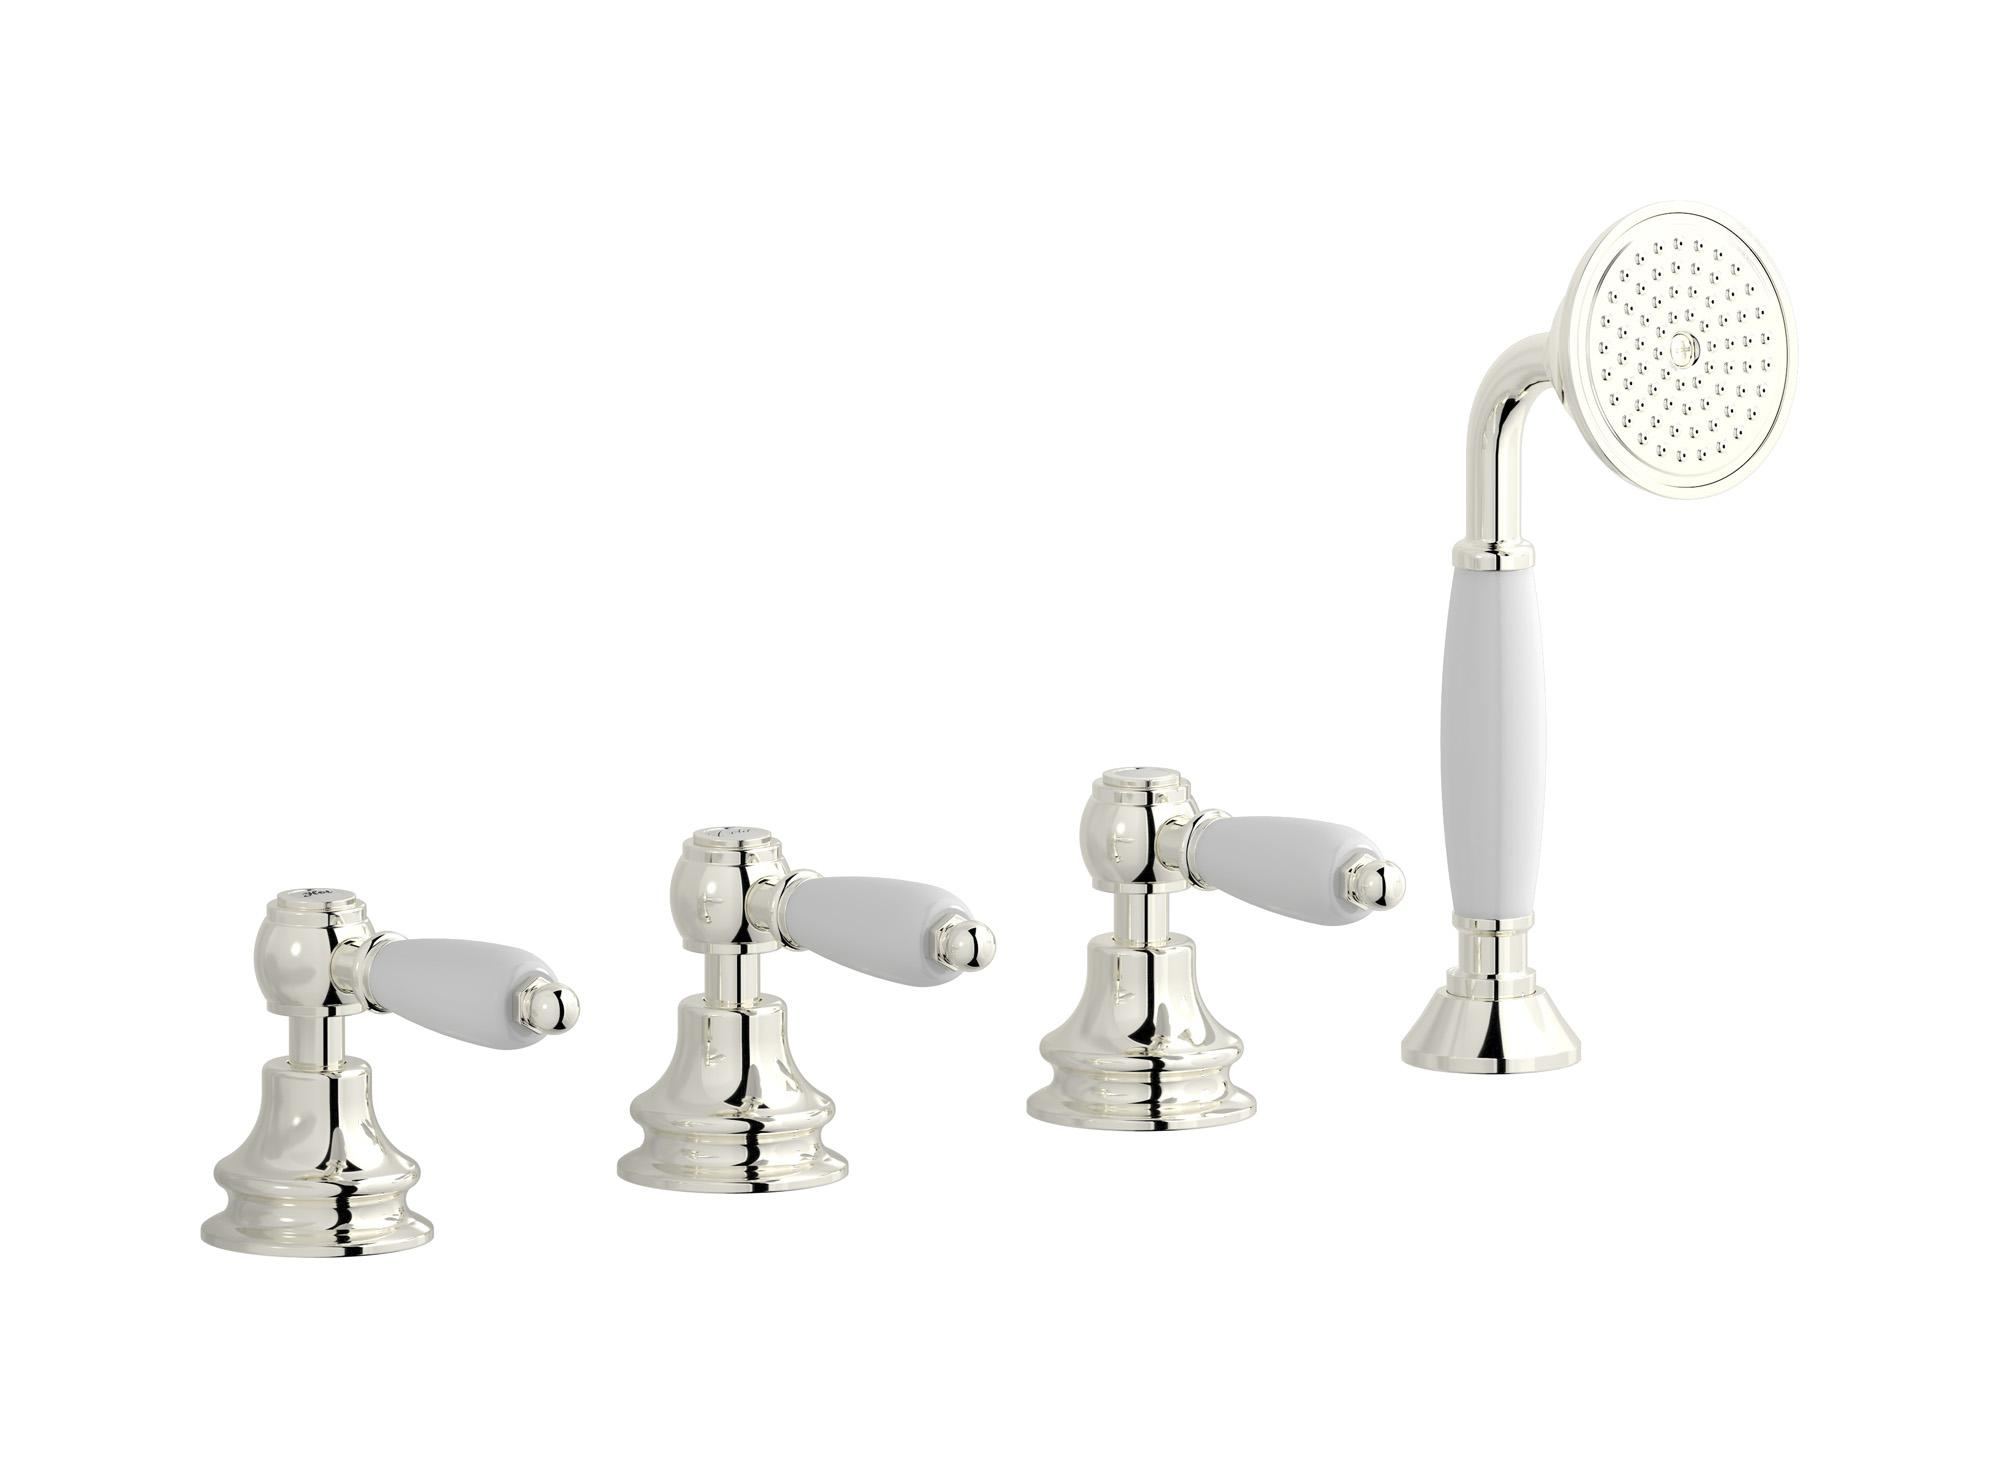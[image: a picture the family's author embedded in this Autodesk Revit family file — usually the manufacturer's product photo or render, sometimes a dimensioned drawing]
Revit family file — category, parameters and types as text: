
# Revit family: HL397_2
name_source: partatom
category: Apparecchi idraulici
units: mm (PartAtom-declared; Revit-internal decimal feet)

## family parameters
Basato su piano di lavoro = No
Condiviso = No
Mantieni orientamento annotazione = No
Numero OmniClass = 23.45.55.17
Punto di calcolo locali = No
Quota connettore circolare = Usa diametro
Sempre verticale = Sì
Taglio con vuoti quando caricato = No
Tipo di parte = Normale
Titolo OmniClass = Mixing Faucets

## types (8) — shared parameters
Cold water inlet = 10 mm  [stored 0.0328084 ft]
Commenti sul tipo = Four holes bath filler with overflow outlet connection, diverter and shower kit
Connessione CW = No
Connessione HW = No
Connessione di scarico = No
Connessione di ventilazione = No
Descrizione = Four holes bath filler with overflow outlet connection, diverter and shower kit
Hot water inlet = 10 mm  [stored 0.0328084 ft]
Produttore = IB Rubinetterie S.p.A.
URL = https://www.weareib.it
zero-valued in all types: Prospetto di default

## per-type parameters (varying)
| type | Finishes surface | Immagine tipo | Modello |
| Chrome | IB_Chrome | HL397CC_2.jpg | HL397CC_2 |
| Antique Bronze | IB_Antique bronze | HL397BB_2.jpg | HL397BB_2 |
| Pale Gold | IB_Pale gold | HL397II_2.jpg | HL397II_2 |
| Brushed Gold | IB_brushed gold | HL397OS_2.jpg | HL397OS_2 |
| Platinum | IB_Platinum | HL397PL_2.jpg | HL397PL_2 |
| Antique Copper | IB_Antique copper | HL397RR_2.jpg | HL397RR_2 |
| Rose Gold | IB_Rose gold | HL397RS_2.jpg | HL397RS_2 |
| Brushed Nickel | IB_Brushed nickel | HL397SS_2.jpg | HL397SS_2 |

note: [stored X ft] marks values corroborated as IEEE doubles in the binary element streams (Revit-internal decimal feet)
